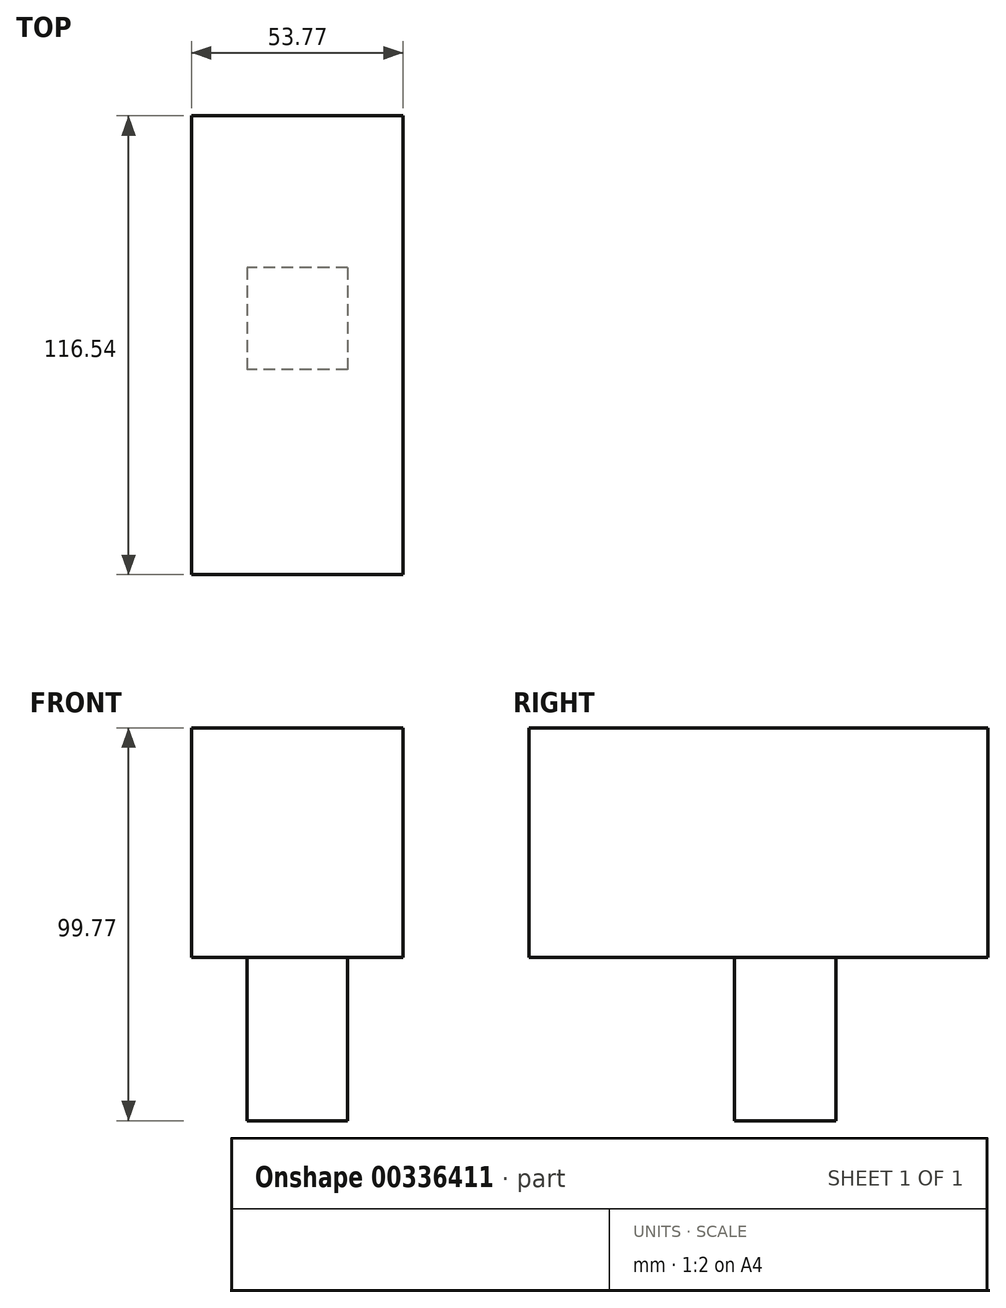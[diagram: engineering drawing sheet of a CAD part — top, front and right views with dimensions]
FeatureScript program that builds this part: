
annotation { "Feature Type Name" : "Feature", "Feature Type Description" : "" }
export const myFeature = defineFeature(function(context is Context, id is Id, definition is map)
    precondition{}
    {
        {
            var Q0;
            Q0=qCreatedBy(makeId("Front.planeOp"),FACE);
            var sketch = newSketch(context, id + "F0", { "sketchPlane" : qUnion([Q0])});
            skLineSegment(sketch, "E0", {"start": v(-53.77, 58.3) * mm, "end": v(-53.77, 0) * mm});
            skLineSegment(sketch, "E1", {"start": v(-53.77, 0) * mm, "end": v(0, 0) * mm});
            skLineSegment(sketch, "E2", {"start": v(0, 0) * mm, "end": v(0, 58.3) * mm});
            skLineSegment(sketch, "E3", {"start": v(0, 58.3) * mm, "end": v(-53.77, 58.3) * mm});
            skSolve(sketch);
        }
        {
            var Q0;
            Q0=makeQuery(id+"F0.imprint","IMPRINT",FACE,{"disambiguationData":[TD([[makeQuery(id+"F0.imprint","IMPRINT",EDGE,{"derivedFrom":sQuery(id+"F0.wireOp",EDGE,"E0")}),1.0]])]});
            extrude(context, id + "F1", {"entities" : qUnion([Q0]), "depth" : 116.54 * mm});
        }
        {
            var Q0;
            Q0=makeQuery(id+"F1.opExtrude","SWEPT_FACE",FACE,{"disambiguationData":[OSD([sQuery(id+"F0.wireOp",EDGE,"E3")])]});
            var sketch = newSketch(context, id + "F2", { "sketchPlane" : qUnion([Q0])});
            skLineSegment(sketch, "E4.bottom", {"start": v(-14.13, -38.58) * mm, "end": v(-39.61, -38.58) * mm});
            skLineSegment(sketch, "E4.top", {"start": v(-14.13, -64.42) * mm, "end": v(-39.61, -64.42) * mm});
            skLineSegment(sketch, "E4.left", {"start": v(-14.13, -38.58) * mm, "end": v(-14.13, -64.42) * mm});
            skLineSegment(sketch, "E4.right", {"start": v(-39.61, -38.58) * mm, "end": v(-39.61, -64.42) * mm});
            skPoint(sketch, "E4.middle", {"position": v(-26.87, -51.5) * mm});
            skSolve(sketch);
        }
        {
            var Q0;
            Q0=makeQuery(id+"F2.imprint","IMPRINT",FACE,{"disambiguationData":[TD([[makeQuery(id+"F2.imprint","IMPRINT",EDGE,{"derivedFrom":sQuery(id+"F2.wireOp",EDGE,"E4.bottom")}),1.0]])]});
            extrude(context, id + "F3", {"entities" : qUnion([Q0]), "operationType" : NewBodyOperationType.ADD, "oppositeDirection" : true, "depth" : 99.77 * mm});
        }
    });
